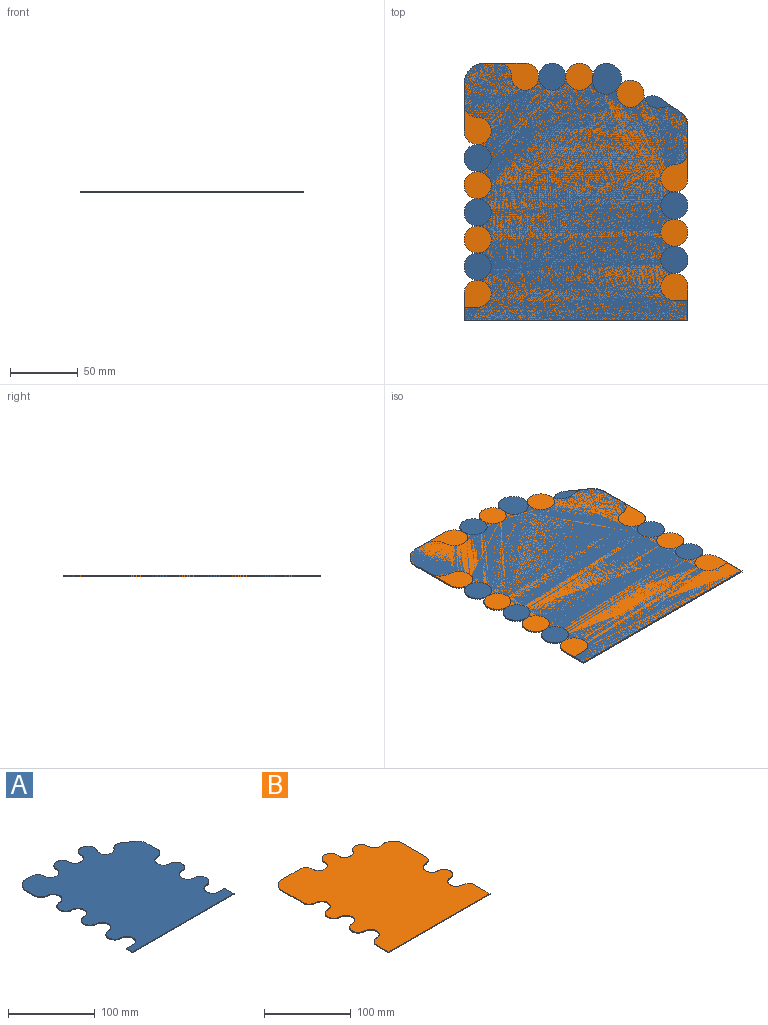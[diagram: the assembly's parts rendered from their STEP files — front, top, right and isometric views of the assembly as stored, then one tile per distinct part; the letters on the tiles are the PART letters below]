
ASSEMBLY  parts=2 mates=1
PART A: 36 faces, bbox 165x190x1 mm
  f0: cylinder r=10mm len=20mm, axis (0,0,-1), area 31.4mm2, adj f1,f33,f34,f35
  f1: cylinder r=10mm len=10mm, axis (0,0,-1), area 15.7mm2, adj f0,f2,f34,f35
  f2: plane 17.19x1mm, normal (1,0,0), area 17.2mm2, adj f1,f3,f34,f35
  f3: cylinder r=15mm len=12.29mm, axis (0,0,-1), area 14.4mm2, adj f2,f4,f34,f35
  f4: plane 13.87x9.71mm, normal (0.57,0.82,0), area 16.9mm2, adj f3,f5,f34,f35
  f5: cylinder r=10mm len=13.93mm, axis (0,0,-1), area 15.7mm2, adj f4,f6,f34,f35
  f6: cylinder r=10mm len=18.19mm, axis (0,0,-1), area 31.4mm2, adj f5,f7,f34,f35
  f7: cylinder r=10mm len=13.93mm, axis (0,0,-1), area 15.7mm2, adj f6,f8,f34,f35
  f8: extruded ~6.97x2.87mm, area 7.7mm2, adj f7,f9,f34,f35
  f9: cylinder r=10mm len=10mm, axis (0,0,-1), area 15.7mm2, adj f8,f10,f34,f35
  f10: cylinder r=10mm len=20mm, axis (0,0,-1), area 31.4mm2, adj f9,f11,f34,f35
  f11: cylinder r=10mm len=20mm, axis (0,0,-1), area 31.4mm2, adj f10,f12,f34,f35
  f12: cylinder r=10mm len=20mm, axis (0,0,-1), area 31.4mm2, adj f11,f13,f34,f35
  f13: cylinder r=10mm len=10mm, axis (0,0,-1), area 15.7mm2, adj f12,f14,f34,f35
  f14: plane 10x1mm, normal (0,1,0), area 10mm2, adj f13,f15,f34,f35
  f15: cylinder r=15mm len=15mm, axis (0,0,-1), area 23.6mm2, adj f14,f16,f34,f35
  f16: plane 15x1mm, normal (-1,0,0), area 15mm2, adj f15,f17,f34,f35
  f17: cylinder r=10mm len=10mm, axis (0,0,-1), area 15.7mm2, adj f16,f18,f34,f35
  f18: cylinder r=10mm len=20mm, axis (0,0,-1), area 31.4mm2, adj f17,f19,f34,f35
  f19: cylinder r=10mm len=20mm, axis (0,0,-1), area 31.4mm2, adj f18,f20,f34,f35
  f20: cylinder r=10mm len=20mm, axis (0,0,-1), area 31.4mm2, adj f19,f21,f34,f35
  f21: cylinder r=10mm len=20mm, axis (0,0,-1), area 31.4mm2, adj f20,f22,f34,f35
  f22: cylinder r=10mm len=20mm, axis (0,0,-1), area 31.4mm2, adj f21,f23,f34,f35
  f23: cylinder r=10mm len=20mm, axis (0,0,-1), area 31.4mm2, adj f22,f24,f34,f35
  f24: cylinder r=10mm len=20mm, axis (0,0,-1), area 31.4mm2, adj f23,f25,f34,f35
  f25: plane 10x1mm, normal (0,1,0), area 10mm2, adj f24,f26,f34,f35
  f26: plane 10x1mm, normal (-1,0,0), area 10mm2, adj f25,f27,f34,f35
  f27: plane 165x1mm, normal (0,-1,0), area 165mm2, adj f26,f28,f34,f35
  f28: plane 15x1mm, normal (1,0,0), area 15mm2, adj f27,f29,f34,f35
  f29: plane 10x1mm, normal (0,1,0), area 10mm2, adj f28,f30,f34,f35
  f30: cylinder r=10mm len=20mm, axis (0,0,-1), area 31.4mm2, adj f29,f31,f34,f35
  f31: cylinder r=10mm len=20mm, axis (0,0,-1), area 31.4mm2, adj f30,f32,f34,f35
  f32: cylinder r=10mm len=20mm, axis (0,0,-1), area 31.4mm2, adj f31,f33,f34,f35
  f33: cylinder r=10mm len=20mm, axis (0,0,-1), area 31.4mm2, adj f0,f32,f34,f35
  f34: plane 190x165mm, normal (0,0,1), area 26191.7mm2, adj f0,f1,f2,f3,f4,f5,f6,f7
  f35: plane 190x165mm, normal (0,0,-1), area 26191.7mm2, adj f0,f1,f2,f3,f4,f5,f6,f7
PART B: 35 faces, bbox 165x190x1 mm
  f0: cylinder r=10mm len=20mm, axis (0,0,-1), area 31.4mm2, adj f1,f32,f33,f34
  f1: cylinder r=10mm len=10mm, axis (0,0,-1), area 15.7mm2, adj f0,f2,f33,f34
  f2: plane 20x1mm, normal (-1,0,0), area 20mm2, adj f1,f3,f33,f34
  f3: plane 165x1mm, normal (0,-1,0), area 165mm2, adj f2,f4,f33,f34
  f4: plane 25x1mm, normal (1,0,0), area 25mm2, adj f3,f5,f33,f34
  f5: cylinder r=10mm len=10mm, axis (0,0,-1), area 15.7mm2, adj f4,f6,f33,f34
  f6: cylinder r=10mm len=20mm, axis (0,0,-1), area 31.4mm2, adj f5,f7,f33,f34
  f7: cylinder r=10mm len=20mm, axis (0,0,-1), area 31.4mm2, adj f6,f8,f33,f34
  f8: cylinder r=10mm len=20mm, axis (0,0,-1), area 31.4mm2, adj f7,f9,f33,f34
  f9: cylinder r=10mm len=10mm, axis (0,0,-1), area 15.7mm2, adj f8,f10,f33,f34
  f10: plane 39.79x1mm, normal (1,0,0), area 39.8mm2, adj f9,f11,f33,f34
  f11: cylinder r=10mm len=8.19mm, axis (0,0,-1), area 9.6mm2, adj f10,f12,f33,f34
  f12: plane 4.42x3.09mm, normal (0.57,0.82,0), area 5.4mm2, adj f11,f13,f33,f34
  f13: cylinder r=10mm len=7.47mm, axis (0,0,-1), area 7.9mm2, adj f12,f14,f33,f34
  f14: plane 4.35x1mm, normal (-0.17,0.98,0), area 4.4mm2, adj f13,f15,f33,f34
  f15: cylinder r=10.13mm len=11.89mm, axis (0,0,-1), area 17.9mm2, adj f14,f16,f33,f34
  f16: cylinder r=10mm len=18.19mm, axis (0,0,-1), area 25.6mm2, adj f15,f17,f33,f34
  f17: plane 1.9x1.33mm, normal (-0.82,0.57,0), area 2.3mm2, adj f16,f18,f33,f34
  f18: cylinder r=10mm len=11.61mm, axis (0,0,-1), area 13.1mm2, adj f17,f19,f33,f34
  f19: plane 1.22x1mm, normal (0.34,0.94,0), area 1.3mm2, adj f18,f20,f33,f34
  f20: cylinder r=8mm len=7.52mm, axis (0,0,-1), area 9.8mm2, adj f19,f21,f33,f34
  f21: plane 4.4x1mm, normal (1,0,0), area 4.4mm2, adj f20,f22,f33,f34
  f22: cylinder r=10mm len=20mm, axis (0,0,-1), area 31.4mm2, adj f21,f23,f33,f34
  f23: cylinder r=10mm len=20mm, axis (0,0,-1), area 31.4mm2, adj f22,f24,f33,f34
  f24: cylinder r=10mm len=10mm, axis (0,0,-1), area 15.7mm2, adj f23,f25,f33,f34
  f25: plane 30x1mm, normal (0,1,0), area 30mm2, adj f24,f26,f33,f34
  f26: cylinder r=15mm len=15mm, axis (0,0,-1), area 23.6mm2, adj f25,f27,f33,f34
  f27: plane 35x1mm, normal (-1,0,0), area 35mm2, adj f26,f28,f33,f34
  f28: cylinder r=10mm len=10mm, axis (0,0,-1), area 15.7mm2, adj f27,f29,f33,f34
  f29: cylinder r=10mm len=20mm, axis (0,0,-1), area 31.4mm2, adj f28,f30,f33,f34
  f30: cylinder r=10mm len=20mm, axis (0,0,-1), area 31.4mm2, adj f29,f31,f33,f34
  f31: cylinder r=10mm len=20mm, axis (0,0,-1), area 31.4mm2, adj f30,f32,f33,f34
  f32: cylinder r=10mm len=20mm, axis (0,0,-1), area 31.4mm2, adj f0,f31,f33,f34
  f33: plane 190x165mm, normal (0,0,1), area 27127.1mm2, adj f0,f1,f2,f3,f4,f5,f6,f7
  f34: plane 190x165mm, normal (0,0,-1), area 27127.1mm2, adj f0,f1,f2,f3,f4,f5,f6,f7
PLACE A t=(-28.8,-47.56,24.15)mm
PLACE B t=(-28.8,-47.56,24.15)mm
MATE planar B.f3 <-> A.f27  axis (0,-1,0) through (53.7,-47.56,24.65)mm
